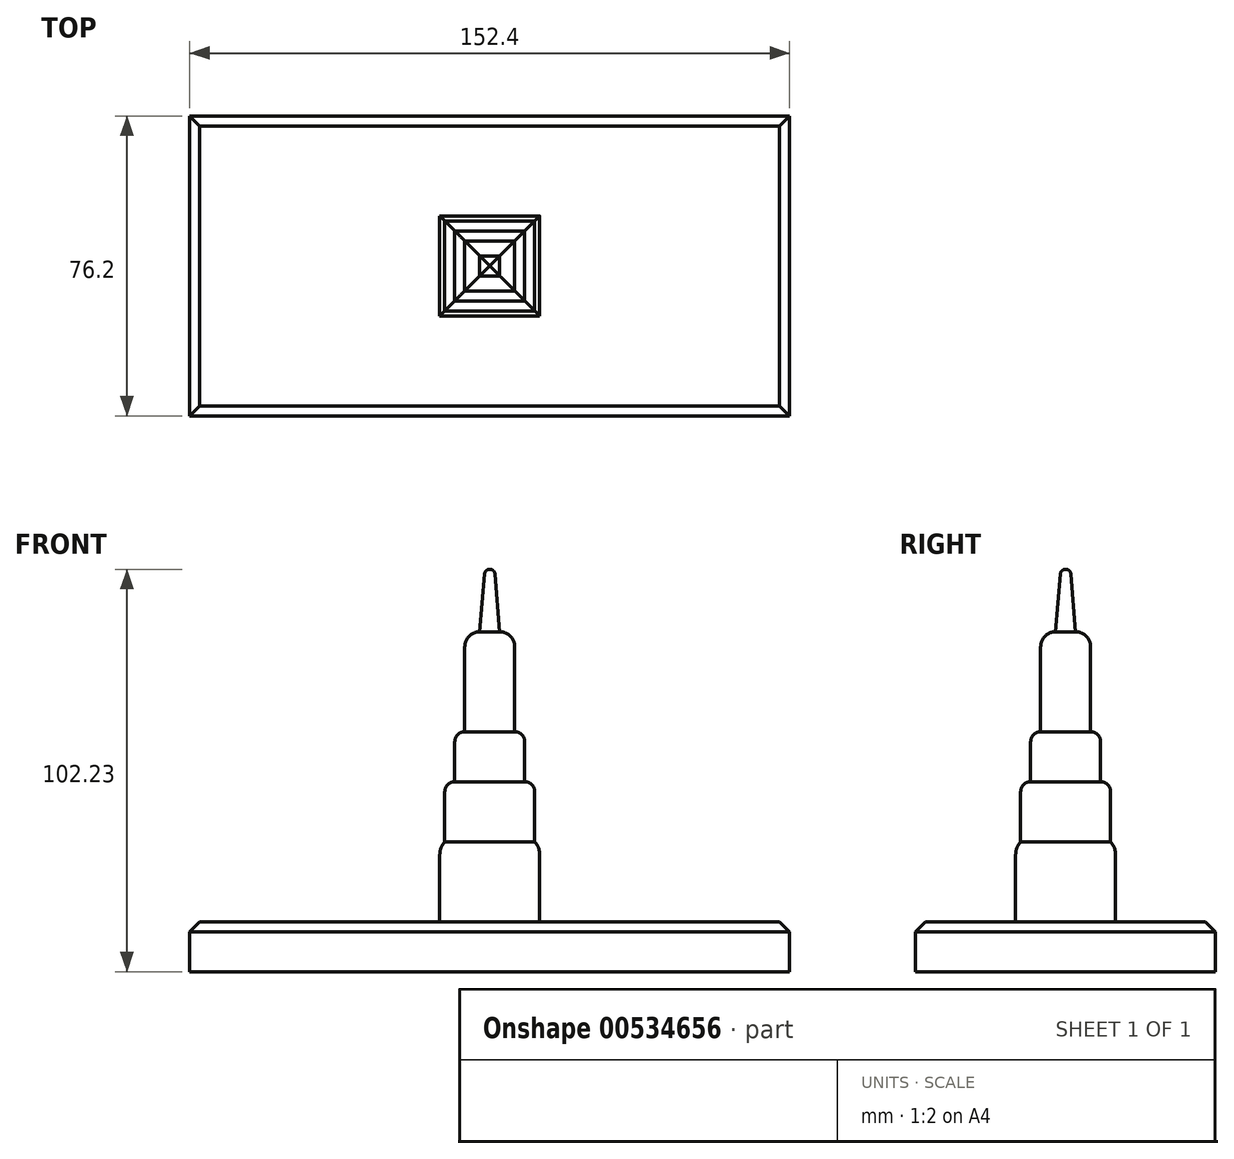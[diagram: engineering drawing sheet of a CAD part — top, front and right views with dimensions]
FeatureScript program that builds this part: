
annotation { "Feature Type Name" : "Feature", "Feature Type Description" : "" }
export const myFeature = defineFeature(function(context is Context, id is Id, definition is map)
    precondition{}
    {
        {
            var Q0;
            Q0=qCreatedBy(makeId("Top.planeOp"),FACE);
            var sketch = newSketch(context, id + "F0", { "sketchPlane" : qUnion([Q0])});
            skLineSegment(sketch, "E0.bottom", {"start": v(76.2, 38.1) * mm, "end": v(-76.2, 38.1) * mm});
            skLineSegment(sketch, "E0.top", {"start": v(76.2, -38.1) * mm, "end": v(-76.2, -38.1) * mm});
            skLineSegment(sketch, "E0.left", {"start": v(76.2, 38.1) * mm, "end": v(76.2, -38.1) * mm});
            skLineSegment(sketch, "E0.right", {"start": v(-76.2, 38.1) * mm, "end": v(-76.2, -38.1) * mm});
            skPoint(sketch, "E0.middle", {"position": v(0, 0) * mm});
            skSolve(sketch);
        }
        {
            var Q0;
            Q0 = qSketchRegion(id + "F0", true);
            extrude(context, id + "F1", {"entities" : qUnion([Q0]), "depth" : 12.7 * mm, "offsetDistance" : 25.4 * mm});
        }
        {
            var Q0;
            Q0=makeQuery(id+"F1.opExtrude","CAP_EDGE",EDGE,{"disambiguationData":[OSD([sQuery(id+"F0.wireOp",EDGE,"E0.top")])],"isStart":false});
            var Q1;
            Q1=makeQuery(id+"F1.opExtrude","CAP_EDGE",EDGE,{"disambiguationData":[OSD([sQuery(id+"F0.wireOp",EDGE,"E0.right")])],"isStart":false});
            var Q2;
            Q2=makeQuery(id+"F1.opExtrude","CAP_EDGE",EDGE,{"disambiguationData":[OSD([sQuery(id+"F0.wireOp",EDGE,"E0.bottom")])],"isStart":false});
            var Q3;
            Q3=makeQuery(id+"F1.opExtrude","CAP_EDGE",EDGE,{"disambiguationData":[OSD([sQuery(id+"F0.wireOp",EDGE,"E0.left")])],"isStart":false});
            chamfer(context, id + "F2", {"entities" : qUnion([Q0, Q1, Q2, Q3]), "width" : 2.54 * mm, "tangentPropagation" : true});
        }
        {
            var Q0;
            Q0=makeQuery(id+"F1.opExtrude","CAP_FACE",FACE,{"disambiguationData":[OSD([sQuery(id+"F0.wireOp",EDGE,"E0.bottom"),sQuery(id+"F0.wireOp",EDGE,"E0.top"),sQuery(id+"F0.wireOp",EDGE,"E0.left"),sQuery(id+"F0.wireOp",EDGE,"E0.right")])],"isStart":false});
            var sketch = newSketch(context, id + "F3", { "sketchPlane" : qUnion([Q0])});
            skLineSegment(sketch, "E1.bottom", {"start": v(12.7, 12.7) * mm, "end": v(-12.7, 12.7) * mm});
            skLineSegment(sketch, "E1.top", {"start": v(12.7, -12.7) * mm, "end": v(-12.7, -12.7) * mm});
            skLineSegment(sketch, "E1.left", {"start": v(12.7, 12.7) * mm, "end": v(12.7, -12.7) * mm});
            skLineSegment(sketch, "E1.right", {"start": v(-12.7, 12.7) * mm, "end": v(-12.7, -12.7) * mm});
            skPoint(sketch, "E1.middle", {"position": v(0, 0) * mm});
            skSolve(sketch);
        }
        {
            var Q0;
            Q0=makeQuery(id+"F3.imprint","IMPRINT",FACE,{"disambiguationData":[TD([[makeQuery(id+"F3.imprint","IMPRINT",EDGE,{"derivedFrom":sQuery(id+"F3.wireOp",EDGE,"E1.bottom")}),1.0]])]});
            extrude(context, id + "F4", {"entities" : qUnion([Q0]), "operationType" : NewBodyOperationType.ADD, "depth" : 20.32 * mm, "offsetDistance" : 25.4 * mm});
        }
        {
            var Q0;
            Q0=makeQuery(id+"F4.opExtrude","CAP_FACE",FACE,{"disambiguationData":[OSD([sQuery(id+"F3.wireOp",EDGE,"E1.bottom"),sQuery(id+"F3.wireOp",EDGE,"E1.top"),sQuery(id+"F3.wireOp",EDGE,"E1.left"),sQuery(id+"F3.wireOp",EDGE,"E1.right")])],"isStart":false});
            var sketch = newSketch(context, id + "F5", { "sketchPlane" : qUnion([Q0])});
            skLineSegment(sketch, "E2.bottom", {"start": v(11.43, -11.43) * mm, "end": v(-11.43, -11.43) * mm});
            skLineSegment(sketch, "E2.top", {"start": v(11.43, 11.43) * mm, "end": v(-11.43, 11.43) * mm});
            skLineSegment(sketch, "E2.left", {"start": v(11.43, -11.43) * mm, "end": v(11.43, 11.43) * mm});
            skLineSegment(sketch, "E2.right", {"start": v(-11.43, -11.43) * mm, "end": v(-11.43, 11.43) * mm});
            skPoint(sketch, "E2.middle", {"position": v(0, 0) * mm});
            skSolve(sketch);
        }
        {
            var Q0;
            Q0=makeQuery(id+"F5.imprint","IMPRINT",FACE,{"disambiguationData":[TD([[makeQuery(id+"F5.imprint","IMPRINT",EDGE,{"derivedFrom":sQuery(id+"F5.wireOp",EDGE,"E2.bottom")}),-1.0]])]});
            extrude(context, id + "F6", {"entities" : qUnion([Q0]), "operationType" : NewBodyOperationType.ADD, "depth" : 15.24 * mm, "offsetDistance" : 25.4 * mm});
        }
        {
            var Q0;
            Q0=makeQuery(id+"F6.opExtrude","CAP_FACE",FACE,{"disambiguationData":[OSD([sQuery(id+"F5.wireOp",EDGE,"E2.bottom"),sQuery(id+"F5.wireOp",EDGE,"E2.top"),sQuery(id+"F5.wireOp",EDGE,"E2.left"),sQuery(id+"F5.wireOp",EDGE,"E2.right")])],"isStart":false});
            var sketch = newSketch(context, id + "F7", { "sketchPlane" : qUnion([Q0])});
            skLineSegment(sketch, "E3.bottom", {"start": v(8.9, -8.89) * mm, "end": v(-8.9, -8.9) * mm});
            skLineSegment(sketch, "E3.top", {"start": v(8.9, 8.9) * mm, "end": v(-8.9, 8.89) * mm});
            skLineSegment(sketch, "E3.left", {"start": v(8.9, -8.89) * mm, "end": v(8.9, 8.9) * mm});
            skLineSegment(sketch, "E3.right", {"start": v(-8.9, -8.9) * mm, "end": v(-8.9, 8.89) * mm});
            skPoint(sketch, "E3.middle", {"position": v(0, 0) * mm});
            skSolve(sketch);
        }
        {
            var Q0;
            Q0=makeQuery(id+"F7.imprint","IMPRINT",FACE,{"disambiguationData":[TD([[makeQuery(id+"F7.imprint","IMPRINT",EDGE,{"derivedFrom":sQuery(id+"F7.wireOp",EDGE,"E3.bottom")}),-1.0]])]});
            extrude(context, id + "F8", {"entities" : qUnion([Q0]), "operationType" : NewBodyOperationType.ADD, "depth" : 12.7 * mm, "offsetDistance" : 25.4 * mm});
        }
        {
            var Q0;
            Q0=makeQuery(id+"F8.opExtrude","CAP_EDGE",EDGE,{"disambiguationData":[OSD([sQuery(id+"F7.wireOp",EDGE,"E3.bottom")])],"isStart":false});
            var Q1;
            Q1=makeQuery(id+"F8.opExtrude","CAP_EDGE",EDGE,{"disambiguationData":[OSD([sQuery(id+"F7.wireOp",EDGE,"E3.left")])],"isStart":false});
            var Q2;
            Q2=makeQuery(id+"F8.opExtrude","CAP_EDGE",EDGE,{"disambiguationData":[OSD([sQuery(id+"F7.wireOp",EDGE,"E3.top")])],"isStart":false});
            var Q3;
            Q3=makeQuery(id+"F8.opExtrude","CAP_EDGE",EDGE,{"disambiguationData":[OSD([sQuery(id+"F7.wireOp",EDGE,"E3.right")])],"isStart":false});
            fillet(context, id + "F9", {"entities" : qUnion([Q0, Q1, Q2, Q3]), "radius" : 2.54 * mm, "tangentPropagation" : true, "allowEdgeOverflow" : false});
        }
        {
            var Q0;
            Q0=makeQuery(id+"F4.opExtrude","CAP_EDGE",EDGE,{"disambiguationData":[OSD([sQuery(id+"F3.wireOp",EDGE,"E1.top")])],"isStart":false});
            var Q1;
            Q1=makeQuery(id+"F4.opExtrude","CAP_EDGE",EDGE,{"disambiguationData":[OSD([sQuery(id+"F3.wireOp",EDGE,"E1.right")])],"isStart":false});
            var Q2;
            Q2=makeQuery(id+"F4.opExtrude","CAP_EDGE",EDGE,{"disambiguationData":[OSD([sQuery(id+"F3.wireOp",EDGE,"E1.left")])],"isStart":false});
            var Q3;
            Q3=makeQuery(id+"F4.opExtrude","CAP_EDGE",EDGE,{"disambiguationData":[OSD([sQuery(id+"F3.wireOp",EDGE,"E1.bottom")])],"isStart":false});
            fillet(context, id + "F10", {"entities" : qUnion([Q0, Q1, Q2, Q3]), "radius" : 5.08 * mm, "tangentPropagation" : true, "allowEdgeOverflow" : false});
        }
        {
            var Q0;
            Q0=makeQuery(id+"F6.opExtrude","CAP_EDGE",EDGE,{"disambiguationData":[OSD([sQuery(id+"F5.wireOp",EDGE,"E2.bottom")])],"isStart":false});
            var Q1;
            Q1=makeQuery(id+"F6.opExtrude","CAP_EDGE",EDGE,{"disambiguationData":[OSD([sQuery(id+"F5.wireOp",EDGE,"E2.right")])],"isStart":false});
            var Q2;
            Q2=makeQuery(id+"F6.opExtrude","CAP_EDGE",EDGE,{"disambiguationData":[OSD([sQuery(id+"F5.wireOp",EDGE,"E2.left")])],"isStart":false});
            var Q3;
            Q3=makeQuery(id+"F6.opExtrude","CAP_EDGE",EDGE,{"disambiguationData":[OSD([sQuery(id+"F5.wireOp",EDGE,"E2.top")])],"isStart":false});
            fillet(context, id + "F11", {"entities" : qUnion([Q0, Q1, Q2, Q3]), "radius" : 2.54 * mm, "tangentPropagation" : true, "allowEdgeOverflow" : false});
        }
        {
            var Q0;
            Q0=makeQuery(id+"F8.opExtrude","CAP_FACE",FACE,{"disambiguationData":[OSD([sQuery(id+"F7.wireOp",EDGE,"E3.bottom"),sQuery(id+"F7.wireOp",EDGE,"E3.top"),sQuery(id+"F7.wireOp",EDGE,"E3.left"),sQuery(id+"F7.wireOp",EDGE,"E3.right")])],"isStart":false});
            extrude(context, id + "F12", {"entities" : qUnion([Q0]), "operationType" : NewBodyOperationType.ADD, "depth" : 25.4 * mm, "offsetDistance" : 25.4 * mm});
        }
        {
            var Q0;
            {var subQ0=sQuery(id+"F7.wireOp",EDGE,"E3.right");var subQ1=sQuery(id+"F7.wireOp",EDGE,"E3.left");var subQ2=sQuery(id+"F7.wireOp",EDGE,"E3.top");var subQ3=sQuery(id+"F7.wireOp",EDGE,"E3.bottom");Q0=makeQuery(id+"F12.opExtrude","CAP_EDGE",EDGE,{"disambiguationData":[OSD([subQ3,subQ2,subQ1,subQ0]),TDD([makeQuery(id+"F9.opFillet","BLEND_EDGE",EDGE,{"blendedFrom":[makeQuery(id+"F8.opExtrude","CAP_EDGE",EDGE,{"disambiguationData":[OSD([subQ2])],"isStart":false}),makeQuery(id+"F8.opExtrude","CAP_FACE",FACE,{"disambiguationData":[OSD([subQ3,subQ2,subQ1,subQ0])],"isStart":false})],"blendedInto":[makeQuery(id+"F8.opExtrude","CAP_FACE",FACE,{"disambiguationData":[OSD([subQ3,subQ2,subQ1,subQ0])],"isStart":false})]})])],"isStart":false});}
            var Q1;
            {var subQ0=sQuery(id+"F7.wireOp",EDGE,"E3.right");var subQ1=sQuery(id+"F7.wireOp",EDGE,"E3.left");var subQ2=sQuery(id+"F7.wireOp",EDGE,"E3.top");var subQ3=sQuery(id+"F7.wireOp",EDGE,"E3.bottom");Q1=makeQuery(id+"F12.opExtrude","CAP_EDGE",EDGE,{"disambiguationData":[OSD([subQ3,subQ2,subQ1,subQ0]),TDD([makeQuery(id+"F9.opFillet","BLEND_EDGE",EDGE,{"blendedFrom":[makeQuery(id+"F8.opExtrude","CAP_EDGE",EDGE,{"disambiguationData":[OSD([subQ1])],"isStart":false}),makeQuery(id+"F8.opExtrude","CAP_FACE",FACE,{"disambiguationData":[OSD([subQ3,subQ2,subQ1,subQ0])],"isStart":false})],"blendedInto":[makeQuery(id+"F8.opExtrude","CAP_FACE",FACE,{"disambiguationData":[OSD([subQ3,subQ2,subQ1,subQ0])],"isStart":false})]})])],"isStart":false});}
            var Q2;
            {var subQ0=sQuery(id+"F7.wireOp",EDGE,"E3.right");var subQ1=sQuery(id+"F7.wireOp",EDGE,"E3.left");var subQ2=sQuery(id+"F7.wireOp",EDGE,"E3.top");var subQ3=sQuery(id+"F7.wireOp",EDGE,"E3.bottom");Q2=makeQuery(id+"F12.opExtrude","CAP_EDGE",EDGE,{"disambiguationData":[OSD([subQ3,subQ2,subQ1,subQ0]),TDD([makeQuery(id+"F9.opFillet","BLEND_EDGE",EDGE,{"blendedFrom":[makeQuery(id+"F8.opExtrude","CAP_EDGE",EDGE,{"disambiguationData":[OSD([subQ3])],"isStart":false}),makeQuery(id+"F8.opExtrude","CAP_FACE",FACE,{"disambiguationData":[OSD([subQ3,subQ2,subQ1,subQ0])],"isStart":false})],"blendedInto":[makeQuery(id+"F8.opExtrude","CAP_FACE",FACE,{"disambiguationData":[OSD([subQ3,subQ2,subQ1,subQ0])],"isStart":false})]})])],"isStart":false});}
            var Q3;
            {var subQ0=sQuery(id+"F7.wireOp",EDGE,"E3.right");var subQ1=sQuery(id+"F7.wireOp",EDGE,"E3.left");var subQ2=sQuery(id+"F7.wireOp",EDGE,"E3.top");var subQ3=sQuery(id+"F7.wireOp",EDGE,"E3.bottom");Q3=makeQuery(id+"F12.opExtrude","CAP_EDGE",EDGE,{"disambiguationData":[OSD([subQ3,subQ2,subQ1,subQ0]),TDD([makeQuery(id+"F9.opFillet","BLEND_EDGE",EDGE,{"blendedFrom":[makeQuery(id+"F8.opExtrude","CAP_EDGE",EDGE,{"disambiguationData":[OSD([subQ0])],"isStart":false}),makeQuery(id+"F8.opExtrude","CAP_FACE",FACE,{"disambiguationData":[OSD([subQ3,subQ2,subQ1,subQ0])],"isStart":false})],"blendedInto":[makeQuery(id+"F8.opExtrude","CAP_FACE",FACE,{"disambiguationData":[OSD([subQ3,subQ2,subQ1,subQ0])],"isStart":false})]})])],"isStart":false});}
            fillet(context, id + "F13", {"entities" : qUnion([Q0, Q1, Q2, Q3]), "radius" : 3.8 * mm, "tangentPropagation" : true, "allowEdgeOverflow" : false});
        }
        {
            var Q0;
            Q0=makeQuery(id+"F12.opExtrude","CAP_FACE",FACE,{"disambiguationData":[OSD([sQuery(id+"F7.wireOp",EDGE,"E3.bottom"),sQuery(id+"F7.wireOp",EDGE,"E3.top"),sQuery(id+"F7.wireOp",EDGE,"E3.left"),sQuery(id+"F7.wireOp",EDGE,"E3.right")])],"isStart":false});
            extrude(context, id + "F14", {"entities" : qUnion([Q0]), "operationType" : NewBodyOperationType.ADD, "depth" : 15.24 * mm, "offsetDistance" : 25.4 * mm});
        }
        {
            var Q0;
            {var subQ0=sQuery(id+"F7.wireOp",EDGE,"E3.right");var subQ1=sQuery(id+"F7.wireOp",EDGE,"E3.left");var subQ2=sQuery(id+"F7.wireOp",EDGE,"E3.top");var subQ3=sQuery(id+"F7.wireOp",EDGE,"E3.bottom");Q0=makeQuery(id+"F14.opExtrude","CAP_EDGE",EDGE,{"disambiguationData":[OSD([subQ3,subQ2,subQ1,subQ0]),TDD([makeQuery(id+"F13.opFillet","BLEND_EDGE",EDGE,{"blendedFrom":[makeQuery(id+"F12.opExtrude","CAP_EDGE",EDGE,{"disambiguationData":[OSD([subQ3,subQ2,subQ1,subQ0]),TDD([makeQuery(id+"F9.opFillet","BLEND_EDGE",EDGE,{"blendedFrom":[makeQuery(id+"F8.opExtrude","CAP_EDGE",EDGE,{"disambiguationData":[OSD([subQ3])],"isStart":false}),makeQuery(id+"F8.opExtrude","CAP_FACE",FACE,{"disambiguationData":[OSD([subQ3,subQ2,subQ1,subQ0])],"isStart":false})],"blendedInto":[makeQuery(id+"F8.opExtrude","CAP_FACE",FACE,{"disambiguationData":[OSD([subQ3,subQ2,subQ1,subQ0])],"isStart":false})]})])],"isStart":false}),makeQuery(id+"F12.opExtrude","CAP_FACE",FACE,{"disambiguationData":[OSD([subQ3,subQ2,subQ1,subQ0])],"isStart":false})],"blendedInto":[makeQuery(id+"F12.opExtrude","CAP_FACE",FACE,{"disambiguationData":[OSD([subQ3,subQ2,subQ1,subQ0])],"isStart":false})]})])],"isStart":false});}
            var Q1;
            {var subQ0=sQuery(id+"F7.wireOp",EDGE,"E3.right");var subQ1=sQuery(id+"F7.wireOp",EDGE,"E3.left");var subQ2=sQuery(id+"F7.wireOp",EDGE,"E3.top");var subQ3=sQuery(id+"F7.wireOp",EDGE,"E3.bottom");Q1=makeQuery(id+"F14.opExtrude","CAP_EDGE",EDGE,{"disambiguationData":[OSD([subQ3,subQ2,subQ1,subQ0]),TDD([makeQuery(id+"F13.opFillet","BLEND_EDGE",EDGE,{"blendedFrom":[makeQuery(id+"F12.opExtrude","CAP_EDGE",EDGE,{"disambiguationData":[OSD([subQ3,subQ2,subQ1,subQ0]),TDD([makeQuery(id+"F9.opFillet","BLEND_EDGE",EDGE,{"blendedFrom":[makeQuery(id+"F8.opExtrude","CAP_EDGE",EDGE,{"disambiguationData":[OSD([subQ0])],"isStart":false}),makeQuery(id+"F8.opExtrude","CAP_FACE",FACE,{"disambiguationData":[OSD([subQ3,subQ2,subQ1,subQ0])],"isStart":false})],"blendedInto":[makeQuery(id+"F8.opExtrude","CAP_FACE",FACE,{"disambiguationData":[OSD([subQ3,subQ2,subQ1,subQ0])],"isStart":false})]})])],"isStart":false}),makeQuery(id+"F12.opExtrude","CAP_FACE",FACE,{"disambiguationData":[OSD([subQ3,subQ2,subQ1,subQ0])],"isStart":false})],"blendedInto":[makeQuery(id+"F12.opExtrude","CAP_FACE",FACE,{"disambiguationData":[OSD([subQ3,subQ2,subQ1,subQ0])],"isStart":false})]})])],"isStart":false});}
            var Q2;
            {var subQ0=sQuery(id+"F7.wireOp",EDGE,"E3.right");var subQ1=sQuery(id+"F7.wireOp",EDGE,"E3.left");var subQ2=sQuery(id+"F7.wireOp",EDGE,"E3.top");var subQ3=sQuery(id+"F7.wireOp",EDGE,"E3.bottom");Q2=makeQuery(id+"F14.opExtrude","CAP_EDGE",EDGE,{"disambiguationData":[OSD([subQ3,subQ2,subQ1,subQ0]),TDD([makeQuery(id+"F13.opFillet","BLEND_EDGE",EDGE,{"blendedFrom":[makeQuery(id+"F12.opExtrude","CAP_EDGE",EDGE,{"disambiguationData":[OSD([subQ3,subQ2,subQ1,subQ0]),TDD([makeQuery(id+"F9.opFillet","BLEND_EDGE",EDGE,{"blendedFrom":[makeQuery(id+"F8.opExtrude","CAP_EDGE",EDGE,{"disambiguationData":[OSD([subQ2])],"isStart":false}),makeQuery(id+"F8.opExtrude","CAP_FACE",FACE,{"disambiguationData":[OSD([subQ3,subQ2,subQ1,subQ0])],"isStart":false})],"blendedInto":[makeQuery(id+"F8.opExtrude","CAP_FACE",FACE,{"disambiguationData":[OSD([subQ3,subQ2,subQ1,subQ0])],"isStart":false})]})])],"isStart":false}),makeQuery(id+"F12.opExtrude","CAP_FACE",FACE,{"disambiguationData":[OSD([subQ3,subQ2,subQ1,subQ0])],"isStart":false})],"blendedInto":[makeQuery(id+"F12.opExtrude","CAP_FACE",FACE,{"disambiguationData":[OSD([subQ3,subQ2,subQ1,subQ0])],"isStart":false})]})])],"isStart":false});}
            var Q3;
            {var subQ0=sQuery(id+"F7.wireOp",EDGE,"E3.right");var subQ1=sQuery(id+"F7.wireOp",EDGE,"E3.left");var subQ2=sQuery(id+"F7.wireOp",EDGE,"E3.top");var subQ3=sQuery(id+"F7.wireOp",EDGE,"E3.bottom");Q3=makeQuery(id+"F14.opExtrude","CAP_EDGE",EDGE,{"disambiguationData":[OSD([subQ3,subQ2,subQ1,subQ0]),TDD([makeQuery(id+"F13.opFillet","BLEND_EDGE",EDGE,{"blendedFrom":[makeQuery(id+"F12.opExtrude","CAP_EDGE",EDGE,{"disambiguationData":[OSD([subQ3,subQ2,subQ1,subQ0]),TDD([makeQuery(id+"F9.opFillet","BLEND_EDGE",EDGE,{"blendedFrom":[makeQuery(id+"F8.opExtrude","CAP_EDGE",EDGE,{"disambiguationData":[OSD([subQ1])],"isStart":false}),makeQuery(id+"F8.opExtrude","CAP_FACE",FACE,{"disambiguationData":[OSD([subQ3,subQ2,subQ1,subQ0])],"isStart":false})],"blendedInto":[makeQuery(id+"F8.opExtrude","CAP_FACE",FACE,{"disambiguationData":[OSD([subQ3,subQ2,subQ1,subQ0])],"isStart":false})]})])],"isStart":false}),makeQuery(id+"F12.opExtrude","CAP_FACE",FACE,{"disambiguationData":[OSD([subQ3,subQ2,subQ1,subQ0])],"isStart":false})],"blendedInto":[makeQuery(id+"F12.opExtrude","CAP_FACE",FACE,{"disambiguationData":[OSD([subQ3,subQ2,subQ1,subQ0])],"isStart":false})]})])],"isStart":false});}
            chamfer(context, id + "F15", {"entities" : qUnion([Q0, Q1, Q2, Q3]), "chamferType" : ChamferType.TWO_OFFSETS, "width1" : 1.27 * mm, "oppositeDirection" : false, "width2" : 15.24 * mm, "tangentPropagation" : true});
        }
        {
            var Q0;
            Q0=makeQuery(id+"F14.opExtrude","CAP_FACE",FACE,{"disambiguationData":[OSD([sQuery(id+"F7.wireOp",EDGE,"E3.bottom"),sQuery(id+"F7.wireOp",EDGE,"E3.top"),sQuery(id+"F7.wireOp",EDGE,"E3.left"),sQuery(id+"F7.wireOp",EDGE,"E3.right")])],"isStart":false});
            extrude(context, id + "F16", {"entities" : qUnion([Q0]), "operationType" : NewBodyOperationType.ADD, "depth" : 0.64 * mm, "offsetDistance" : 25.4 * mm});
        }
        {
            var Q0;
            {var subQ0=sQuery(id+"F7.wireOp",EDGE,"E3.right");var subQ1=sQuery(id+"F7.wireOp",EDGE,"E3.left");var subQ2=sQuery(id+"F7.wireOp",EDGE,"E3.top");var subQ3=sQuery(id+"F7.wireOp",EDGE,"E3.bottom");Q0=makeQuery(id+"F16.opExtrude","CAP_EDGE",EDGE,{"disambiguationData":[OSD([subQ3,subQ2,subQ1,subQ0]),TDD([makeQuery(id+"F15.opChamfer","BLEND_EDGE",EDGE,{"blendedFrom":[makeQuery(id+"F14.opExtrude","CAP_EDGE",EDGE,{"disambiguationData":[OSD([subQ3,subQ2,subQ1,subQ0]),TDD([makeQuery(id+"F13.opFillet","BLEND_EDGE",EDGE,{"blendedFrom":[makeQuery(id+"F12.opExtrude","CAP_EDGE",EDGE,{"disambiguationData":[OSD([subQ3,subQ2,subQ1,subQ0]),TDD([makeQuery(id+"F9.opFillet","BLEND_EDGE",EDGE,{"blendedFrom":[makeQuery(id+"F8.opExtrude","CAP_EDGE",EDGE,{"disambiguationData":[OSD([subQ2])],"isStart":false}),makeQuery(id+"F8.opExtrude","CAP_FACE",FACE,{"disambiguationData":[OSD([subQ3,subQ2,subQ1,subQ0])],"isStart":false})],"blendedInto":[makeQuery(id+"F8.opExtrude","CAP_FACE",FACE,{"disambiguationData":[OSD([subQ3,subQ2,subQ1,subQ0])],"isStart":false})]})])],"isStart":false}),makeQuery(id+"F12.opExtrude","CAP_FACE",FACE,{"disambiguationData":[OSD([subQ3,subQ2,subQ1,subQ0])],"isStart":false})],"blendedInto":[makeQuery(id+"F12.opExtrude","CAP_FACE",FACE,{"disambiguationData":[OSD([subQ3,subQ2,subQ1,subQ0])],"isStart":false})]})])],"isStart":false}),makeQuery(id+"F14.opExtrude","CAP_FACE",FACE,{"disambiguationData":[OSD([subQ3,subQ2,subQ1,subQ0])],"isStart":false})],"blendedInto":[makeQuery(id+"F14.opExtrude","CAP_FACE",FACE,{"disambiguationData":[OSD([subQ3,subQ2,subQ1,subQ0])],"isStart":false})]})])],"isStart":false});}
            var Q1;
            {var subQ0=sQuery(id+"F7.wireOp",EDGE,"E3.right");var subQ1=sQuery(id+"F7.wireOp",EDGE,"E3.left");var subQ2=sQuery(id+"F7.wireOp",EDGE,"E3.top");var subQ3=sQuery(id+"F7.wireOp",EDGE,"E3.bottom");Q1=makeQuery(id+"F16.opExtrude","CAP_EDGE",EDGE,{"disambiguationData":[OSD([subQ3,subQ2,subQ1,subQ0]),TDD([makeQuery(id+"F15.opChamfer","BLEND_EDGE",EDGE,{"blendedFrom":[makeQuery(id+"F14.opExtrude","CAP_EDGE",EDGE,{"disambiguationData":[OSD([subQ3,subQ2,subQ1,subQ0]),TDD([makeQuery(id+"F13.opFillet","BLEND_EDGE",EDGE,{"blendedFrom":[makeQuery(id+"F12.opExtrude","CAP_EDGE",EDGE,{"disambiguationData":[OSD([subQ3,subQ2,subQ1,subQ0]),TDD([makeQuery(id+"F9.opFillet","BLEND_EDGE",EDGE,{"blendedFrom":[makeQuery(id+"F8.opExtrude","CAP_EDGE",EDGE,{"disambiguationData":[OSD([subQ0])],"isStart":false}),makeQuery(id+"F8.opExtrude","CAP_FACE",FACE,{"disambiguationData":[OSD([subQ3,subQ2,subQ1,subQ0])],"isStart":false})],"blendedInto":[makeQuery(id+"F8.opExtrude","CAP_FACE",FACE,{"disambiguationData":[OSD([subQ3,subQ2,subQ1,subQ0])],"isStart":false})]})])],"isStart":false}),makeQuery(id+"F12.opExtrude","CAP_FACE",FACE,{"disambiguationData":[OSD([subQ3,subQ2,subQ1,subQ0])],"isStart":false})],"blendedInto":[makeQuery(id+"F12.opExtrude","CAP_FACE",FACE,{"disambiguationData":[OSD([subQ3,subQ2,subQ1,subQ0])],"isStart":false})]})])],"isStart":false}),makeQuery(id+"F14.opExtrude","CAP_FACE",FACE,{"disambiguationData":[OSD([subQ3,subQ2,subQ1,subQ0])],"isStart":false})],"blendedInto":[makeQuery(id+"F14.opExtrude","CAP_FACE",FACE,{"disambiguationData":[OSD([subQ3,subQ2,subQ1,subQ0])],"isStart":false})]})])],"isStart":false});}
            var Q2;
            {var subQ0=sQuery(id+"F7.wireOp",EDGE,"E3.right");var subQ1=sQuery(id+"F7.wireOp",EDGE,"E3.left");var subQ2=sQuery(id+"F7.wireOp",EDGE,"E3.top");var subQ3=sQuery(id+"F7.wireOp",EDGE,"E3.bottom");Q2=makeQuery(id+"F16.opExtrude","CAP_EDGE",EDGE,{"disambiguationData":[OSD([subQ3,subQ2,subQ1,subQ0]),TDD([makeQuery(id+"F15.opChamfer","BLEND_EDGE",EDGE,{"blendedFrom":[makeQuery(id+"F14.opExtrude","CAP_EDGE",EDGE,{"disambiguationData":[OSD([subQ3,subQ2,subQ1,subQ0]),TDD([makeQuery(id+"F13.opFillet","BLEND_EDGE",EDGE,{"blendedFrom":[makeQuery(id+"F12.opExtrude","CAP_EDGE",EDGE,{"disambiguationData":[OSD([subQ3,subQ2,subQ1,subQ0]),TDD([makeQuery(id+"F9.opFillet","BLEND_EDGE",EDGE,{"blendedFrom":[makeQuery(id+"F8.opExtrude","CAP_EDGE",EDGE,{"disambiguationData":[OSD([subQ3])],"isStart":false}),makeQuery(id+"F8.opExtrude","CAP_FACE",FACE,{"disambiguationData":[OSD([subQ3,subQ2,subQ1,subQ0])],"isStart":false})],"blendedInto":[makeQuery(id+"F8.opExtrude","CAP_FACE",FACE,{"disambiguationData":[OSD([subQ3,subQ2,subQ1,subQ0])],"isStart":false})]})])],"isStart":false}),makeQuery(id+"F12.opExtrude","CAP_FACE",FACE,{"disambiguationData":[OSD([subQ3,subQ2,subQ1,subQ0])],"isStart":false})],"blendedInto":[makeQuery(id+"F12.opExtrude","CAP_FACE",FACE,{"disambiguationData":[OSD([subQ3,subQ2,subQ1,subQ0])],"isStart":false})]})])],"isStart":false}),makeQuery(id+"F14.opExtrude","CAP_FACE",FACE,{"disambiguationData":[OSD([subQ3,subQ2,subQ1,subQ0])],"isStart":false})],"blendedInto":[makeQuery(id+"F14.opExtrude","CAP_FACE",FACE,{"disambiguationData":[OSD([subQ3,subQ2,subQ1,subQ0])],"isStart":false})]})])],"isStart":false});}
            var Q3;
            {var subQ0=sQuery(id+"F7.wireOp",EDGE,"E3.right");var subQ1=sQuery(id+"F7.wireOp",EDGE,"E3.left");var subQ2=sQuery(id+"F7.wireOp",EDGE,"E3.top");var subQ3=sQuery(id+"F7.wireOp",EDGE,"E3.bottom");Q3=makeQuery(id+"F16.opExtrude","CAP_EDGE",EDGE,{"disambiguationData":[OSD([subQ3,subQ2,subQ1,subQ0]),TDD([makeQuery(id+"F15.opChamfer","BLEND_EDGE",EDGE,{"blendedFrom":[makeQuery(id+"F14.opExtrude","CAP_EDGE",EDGE,{"disambiguationData":[OSD([subQ3,subQ2,subQ1,subQ0]),TDD([makeQuery(id+"F13.opFillet","BLEND_EDGE",EDGE,{"blendedFrom":[makeQuery(id+"F12.opExtrude","CAP_EDGE",EDGE,{"disambiguationData":[OSD([subQ3,subQ2,subQ1,subQ0]),TDD([makeQuery(id+"F9.opFillet","BLEND_EDGE",EDGE,{"blendedFrom":[makeQuery(id+"F8.opExtrude","CAP_EDGE",EDGE,{"disambiguationData":[OSD([subQ1])],"isStart":false}),makeQuery(id+"F8.opExtrude","CAP_FACE",FACE,{"disambiguationData":[OSD([subQ3,subQ2,subQ1,subQ0])],"isStart":false})],"blendedInto":[makeQuery(id+"F8.opExtrude","CAP_FACE",FACE,{"disambiguationData":[OSD([subQ3,subQ2,subQ1,subQ0])],"isStart":false})]})])],"isStart":false}),makeQuery(id+"F12.opExtrude","CAP_FACE",FACE,{"disambiguationData":[OSD([subQ3,subQ2,subQ1,subQ0])],"isStart":false})],"blendedInto":[makeQuery(id+"F12.opExtrude","CAP_FACE",FACE,{"disambiguationData":[OSD([subQ3,subQ2,subQ1,subQ0])],"isStart":false})]})])],"isStart":false}),makeQuery(id+"F14.opExtrude","CAP_FACE",FACE,{"disambiguationData":[OSD([subQ3,subQ2,subQ1,subQ0])],"isStart":false})],"blendedInto":[makeQuery(id+"F14.opExtrude","CAP_FACE",FACE,{"disambiguationData":[OSD([subQ3,subQ2,subQ1,subQ0])],"isStart":false})]})])],"isStart":false});}
            fillet(context, id + "F17", {"entities" : qUnion([Q0, Q1, Q2, Q3]), "radius" : 1.27 * mm, "tangentPropagation" : true, "allowEdgeOverflow" : false});
        }
    });
